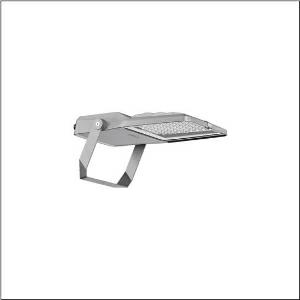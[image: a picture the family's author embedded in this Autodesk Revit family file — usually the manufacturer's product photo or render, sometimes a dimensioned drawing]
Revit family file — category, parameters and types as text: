
# Revit family: floodlight_fl_21_mini___pl61_5xa7775d2c1a_9234
name_source: partatom
category: Lighting Fixtures
units: mm (PartAtom-declared; Revit-internal decimal feet)

## family parameters
Cut with Voids When Loaded = No
Host = Face
Light Source = No
Part Type = Normal
Room Calculation Point = No
Round Connector Dimension = Use Diameter
Shared = No

## types (1)
- --- (1 x LED, 17510 lm, 142.9 W, 3000K)
    Apparent Load = 143 VA
    CIE Flux Codes = 33 65 98 100 100
    Color Rendering = 70
    Color Temperature = 3000K
    Default Elevation = 1800 mm
    Description = Floodlight FL 21 mini, floodlight, primary light control with lens, of PMMA, primary optical cover: protective disc, of toughened safety glass, transparent, light distribution: PL61, light emission: direct distribution, installation type: surface-mounted, LED, High Power LED, rated luminous flux: 17.510lm, luminous efficacy: 123lm/W, light colour: 730, colour temperature: 3000K, control gear: Smart Interface (Zhaga), control: flexible luminous flux parameterisation, time-dependent luminous flux control, constant luminous flux control, overheat protection, pre-setting: logarithmic dimming characteristic, with terminal, 6-pole, mains connection: 220..240V, AC, 50/60Hz, start of lifetime: 143W, end of service life: 151W, reduction: 63W, luminaire housing, of diecast aluminium, powder-coated, Siteco® metallic grey (DB 702S), corrosivity category C5 mid according to DIN EN ISO 12944, suitable for swimming pools, chlorine-resistant, sealing non-destructively replaceable, mounting bracket, of steel, galvanised, powder-coated, Siteco® metallic grey (DB 702S), Smart Interface above, protection rating (complete): IP66, insulation class (complete): insulation class II (safety insulation), certification: CE, ENEC, VDE, protection symbol: D, impact resistance: IK08, permissible operating ambient temperature: -40..+40°C, permissible operating ambient temperature for outdoor applications: -40..+50°C, standard: DIN EN 12944, LABS conformity tested according to VDMA 24364:2018-05, packaging unit: 1 piece

Light Distribution: PL61
    Height = 70 mm
    Lamp = 1 x LED
    Lamp Light Flux = 17510 lm
    Lamp Power = 142.9 W
    Lamp count = 1
    Length = 485 mm
    Luminous efficacy = 123 lm/W
    Manufacturer = Siteco
    ModVariant = No
    Model = 5XA7775D2C1A
    Number of Poles = 1
    OnlyDefault = Yes
    Power Factor = 1
    Product Name = Floodlight FL 21 mini | PL61
    Product group = floodlight | pylon annexe
    ProductGroupID = 6200
    Protection Class = Protection class II
    Protection Degree = IP 66
    RLX_Detail_Level = 1
    RLX_Emergency_Light_Flux = 0 lm
    RLX_Emergency_Type = 0
    RLX_Emergency_Type_DB = No
    RlxData = <blob elided: 96329 chars, md5=cdaf1542>
    Socket = socket
    Standby Power = 0 W
    System Light Flux = 17510 lm
    System Power = 143 W
    Type Comments = factory setting: luminous flux: 100 % | dim-lin: 254 | 730 mA
    Type Image = l_1006845.jpg
    URL = http://relux.com
    VarID = @adj_171962
    Voltage = 0 V
    Weight = 0.00 kg
    Width = 337 mm

## geometry (parser evidence)
native form markers: Blend x4, Sweep x14
no freeform markers — native parametric forms only
